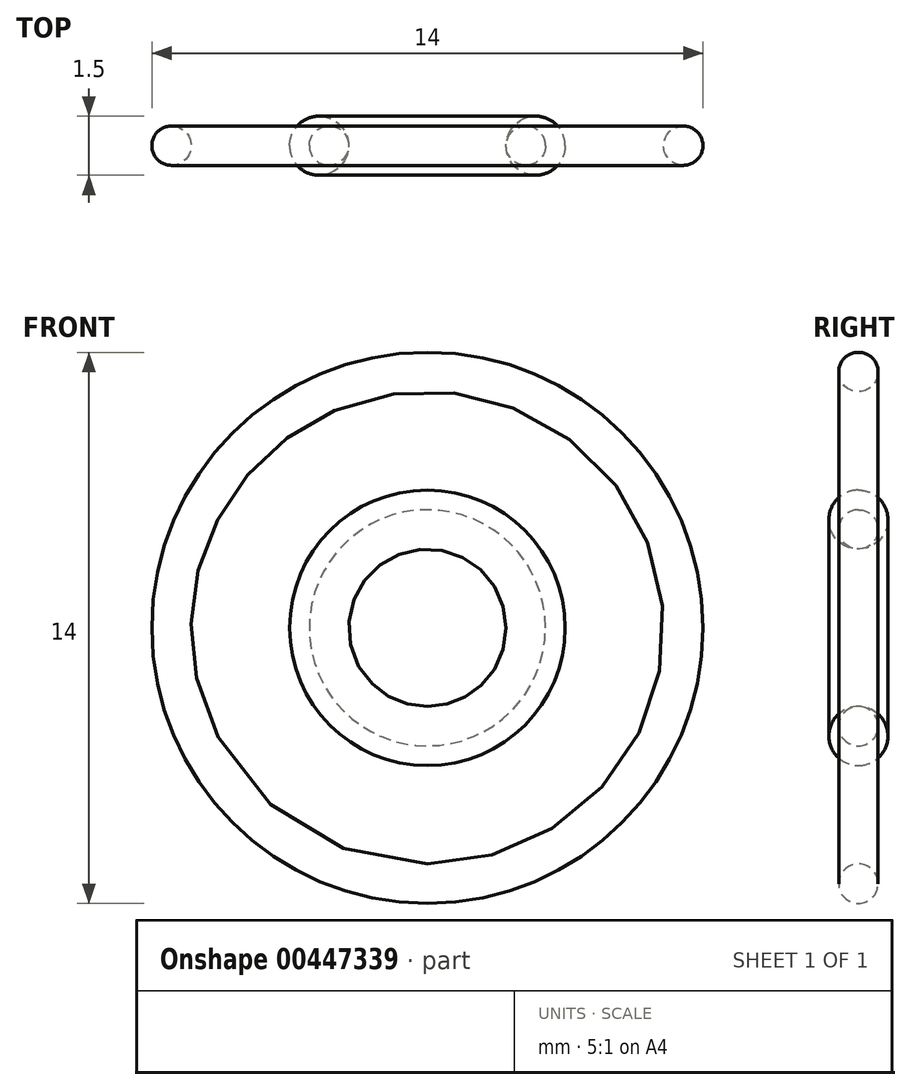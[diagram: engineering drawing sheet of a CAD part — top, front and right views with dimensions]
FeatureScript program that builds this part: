
annotation { "Feature Type Name" : "Feature", "Feature Type Description" : "" }
export const myFeature = defineFeature(function(context is Context, id is Id, definition is map)
    precondition{}
    {
        {
            var Q0;
            Q0=qCreatedBy(makeId("Right.planeOp"),FACE);
            var sketch = newSketch(context, id + "F0", { "sketchPlane" : qUnion([Q0])});
            skLineSegment(sketch, "E0", {"start": v(0, 0) * mm, "end": v(0, 6.5) * mm, "construction": true});
            skCircle(sketch, "E1", {"center": v(0, 6.5) * mm, "radius": 0.5 * mm});
            skCircle(sketch, "E2", {"center": v(0, 2.75) * mm, "radius": 0.75 * mm});
            skCircle(sketch, "E3", {"center": v(0, -2.5) * mm, "radius": 0.5 * mm});
            skSolve(sketch);
        }
        {
            var Q0;
            Q0=qCreatedBy(makeId("Top.planeOp"),FACE);
            var sketch = newSketch(context, id + "F1", { "sketchPlane" : qUnion([Q0])});
            skLineSegment(sketch, "E4", {"start": v(0, 0) * mm, "end": v(0, 14.88) * mm, "construction": true});
            skSolve(sketch);
        }
        {
            var Q0;
            Q0=makeQuery(id+"F0.imprint","IMPRINT",FACE,{"disambiguationData":[TD([[makeQuery(id+"F0.imprint","IMPRINT",EDGE,{"derivedFrom":sQuery(id+"F0.wireOp",EDGE,"E1")}),1.0]])]});
            var Q1;
            Q1=sQuery(id+"F1.wireOp",EDGE,"E4");
            revolve(context, id + "F2", {"entities" : qUnion([Q0]), "axis" : qUnion([Q1]), "revolveType" : RevolveType.FULL});
        }
        {
            var Q0;
            Q0=makeQuery(id+"F0.imprint","IMPRINT",FACE,{"disambiguationData":[TD([[makeQuery(id+"F0.imprint","IMPRINT",EDGE,{"derivedFrom":sQuery(id+"F0.wireOp",EDGE,"E2")}),1.0]])]});
            var Q1;
            Q1=sQuery(id+"F1.wireOp",EDGE,"E4");
            revolve(context, id + "F3", {"entities" : qUnion([Q0]), "axis" : qUnion([Q1]), "revolveType" : RevolveType.FULL});
        }
        {
            var Q0;
            Q0=makeQuery(id+"F0.imprint","IMPRINT",FACE,{"disambiguationData":[TD([[makeQuery(id+"F0.imprint","IMPRINT",EDGE,{"derivedFrom":sQuery(id+"F0.wireOp",EDGE,"E3")}),1.0]])]});
            var Q1;
            Q1=sQuery(id+"F1.wireOp",EDGE,"E4");
            revolve(context, id + "F4", {"entities" : qUnion([Q0]), "axis" : qUnion([Q1]), "revolveType" : RevolveType.FULL});
        }
    });
